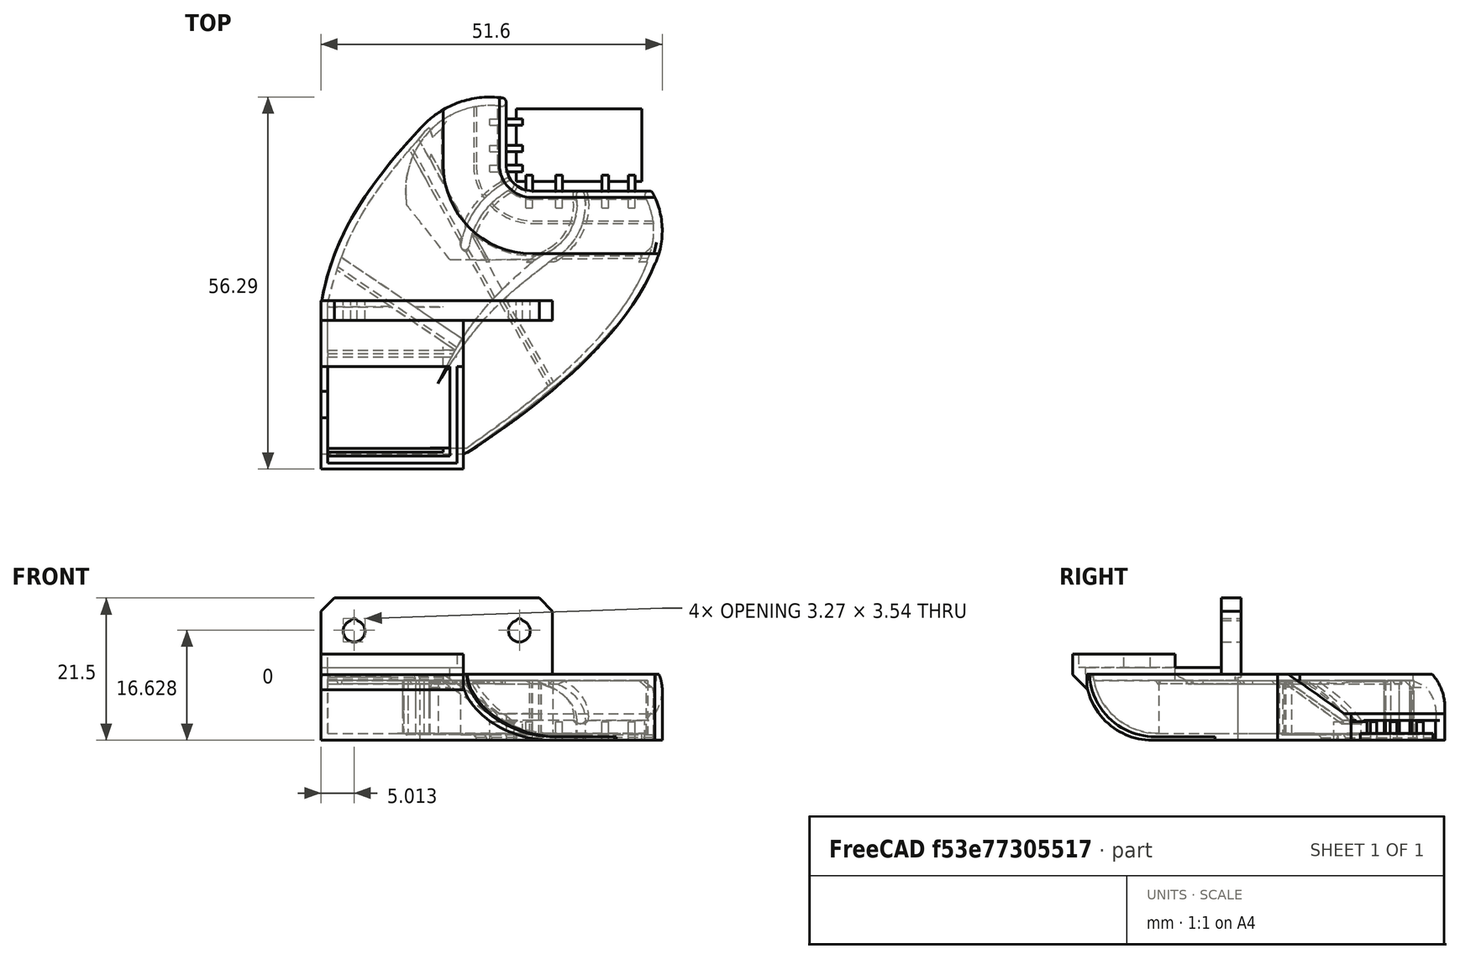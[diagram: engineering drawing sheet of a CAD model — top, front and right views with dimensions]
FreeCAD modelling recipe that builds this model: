
FCSTD DOCUMENT  (FreeCAD 0.18R16146 (Git))
Label: titanduct-v6-block
License: All rights reserved
LicenseURL: http://en.wikipedia.org/wiki/All_rights_reserved
objects: Part::Box×43, Part::Cut×25, Part::Feature×15, Part::MultiFuse×13, Part::Chamfer×10, Part::Cylinder×6, Part::Fillet×6
note: 118 computed .brp shape members not serialized (recipe doc carries the construction recipe); baked Part::Feature solids carry a one-line shape summary decoded from their .brp

FEATURE [Part::Feature] Part__Feature034001  label="duct001"
  Placement = pos=(4.485,21.775,-6.0908e-11) rot=(0,0,-1;0.785398rad)
  shape: bbox 54.56 x 52.76 x 17.07 mm, 140 faces (baked)
FEATURE [Part::Box] Box  label="Cube"
  AttacherType = Attacher::AttachEngine3D
  Height = 10
  Length = 42
  Placement = pos=(-35,-33,10) rot=(0,0,1;0rad)
  Width = 47
FEATURE [Part::Cut] Cut
  Base = -> Part__Feature034001
  Tool = -> Box
FEATURE [Part::Box] Box001  label="Cube001"
  AttacherType = Attacher::AttachEngine3D
  Height = 31
  Length = 50
  Placement = pos=(-35,-32,-4) rot=(0,0,1;0rad)
  Width = 31
FEATURE [Part::Cut] Cut001
  Base = -> Cut
  Tool = -> Box001
FEATURE [Part::Box] Box002  label="Cube002"
  AttacherType = Attacher::AttachEngine3D
  Height = 16
  Length = 10
  Placement = pos=(-33.8,-4,0) rot=(0,0,1;0rad)
  Width = 10
FEATURE [Part::Cut] Cut002
  Base = -> Cut001
  Placement = pos=(-2.5,3.3,-9) rot=(0,0,1;0rad)
  Tool = -> Box002
FEATURE [Part::Box] Box005  label="Cube005"
  AttacherType = Attacher::AttachEngine3D
  Height = 10
  Length = 35
  Width = 3
FEATURE [Part::Cylinder] Cylinder
  Angle = 360
  AttacherType = Attacher::AttachEngine3D
  Height = 10
  Placement = pos=(5,1e-15,5) rot=(-1,0,0;1.5708rad)
  Radius = 1.65
FEATURE [Part::Cylinder] Cylinder001
  Angle = 360
  AttacherType = Attacher::AttachEngine3D
  Height = 10
  Placement = pos=(30,1e-15,5) rot=(-1,0,0;1.5708rad)
  Radius = 1.65
FEATURE [Part::Cylinder] Cylinder002
  Angle = 360
  AttacherType = Attacher::AttachEngine3D
  Height = 10
  Placement = pos=(30,1e-15,5) rot=(-1,0,0;1.5708rad)
  Radius = 0.5
FEATURE [Part::Cylinder] Cylinder003
  Angle = 360
  AttacherType = Attacher::AttachEngine3D
  Height = 10
  Placement = pos=(5,1e-15,5) rot=(-1,0,0;1.5708rad)
  Radius = 0.5
FEATURE [Part::MultiFuse] Fusion001
  Shapes = -> [Cylinder001,Cylinder]
FEATURE [Part::MultiFuse] Fusion002
  Placement = pos=(0,0,1.4) rot=(0,0,1;0rad)
  Shapes = -> [Cylinder003,Cylinder002]
FEATURE [Part::MultiFuse] Fusion003
  Shapes = -> [Fusion002,Fusion001]
FEATURE [Part::Chamfer] Chamfer001
  Base = -> Box005
  Edges = 2 edges r=2: [Edge2,Edge6]
FEATURE [Part::Cut] Cut003  label="mounter"
  Base = -> Chamfer001
  Placement = pos=(-38,-6.5,11) rot=(0,0,1;0rad)
  Tool = -> Fusion003
FEATURE [Part::Box] Box014  label="Cube014"
  AttacherType = Attacher::AttachEngine3D
  Height = 3
  Length = 1
  Placement = pos=(-38,-29,9.5) rot=(0,0,1;0rad)
  Width = 7.75
FEATURE [Part::Box] Box015  label="Cube015"
  AttacherType = Attacher::AttachEngine3D
  Height = 3
  Length = 1
  Placement = pos=(-38,-17.25,9.5) rot=(0,0,1;0rad)
  Width = 3.75
FEATURE [Part::Box] Box016  label="Cube016"
  AttacherType = Attacher::AttachEngine3D
  Height = 1
  Length = 21.5
  Placement = pos=(-2.5,-38,-1) rot=(0,0,1;0rad)
  Width = 18.5
FEATURE [Part::Box] Box017  label="Cube017"
  AttacherType = Attacher::AttachEngine3D
  Height = 1.5
  Length = 21.5
  Placement = pos=(-38,-11.5,9) rot=(0,0,1;0rad)
  Width = 8
FEATURE [Part::Box] Box018  label="Cube018"
  AttacherType = Attacher::AttachEngine3D
  Height = 1
  Length = 18.5
  Placement = pos=(-1.5,-36,-1) rot=(0,0,1;0rad)
  Width = 13.5
FEATURE [Part::Feature] Body001001  label="Body002"
  Placement = pos=(0,0,-9) rot=(0,0,1;0rad)
  shape: bbox 32 x 33 x 12 mm, 6 faces (baked)
FEATURE [Part::Feature] Body001002  label="Body003"
  Placement = pos=(0,0,-9) rot=(0,0,1;0rad)
  shape: bbox 16 x 26.5 x 13 mm, 6 faces (baked)
FEATURE [Part::Box] Box021  label="Cube021"
  AttacherType = Attacher::AttachEngine3D
  Height = 18
  Length = 52
  Placement = pos=(-38,-28,-9) rot=(0,0,1;0rad)
  Width = 2
FEATURE [Part::Box] Box022  label="Cube022"
  AttacherType = Attacher::AttachEngine3D
  Height = 1
  Length = 52
  Placement = pos=(-38,-27,-9) rot=(0,0,1;0rad)
  Width = 20
FEATURE [Part::Feature] Fusion004002003
  shape: bbox 52 x 20 x 18 mm, 8 faces (baked)
FEATURE [Part::Fillet] Fillet
  Base = -> Fusion004002003
  Edges = 1 edges r=10: [Edge7]
FEATURE [Part::Fillet] Fillet002
  Base = -> Fillet
  Edges = 1 edges r=10: [Edge21]
FEATURE [Part::MultiFuse] Fusion
  Shapes = -> [Box021,Box022]
FEATURE [Part::Fillet] Fillet003
  Base = -> Fusion
  Edges = 1 edges r=10: [Edge11]
  Placement = pos=(0,-0.5,-0.5) rot=(0,0,1;0rad)
FEATURE [Part::Feature] Fillet003001  label="Fillet004"
  Placement = pos=(0,-0.5,-0.5) rot=(0,0,1;0rad)
  shape: bbox 52 x 21 x 18 mm, 15 faces (baked)
FEATURE [Part::Cut] Cut005
  Base = -> Body001001
  Tool = -> Fillet003001
FEATURE [Part::Box] Box023  label="Cube023"
  AttacherType = Attacher::AttachEngine3D
  Height = 18
  Length = 1
  Placement = pos=(-38,-27,-9) rot=(0,0,1;0rad)
  Width = 23
FEATURE [Part::Box] Box024  label="Cube024"
  AttacherType = Attacher::AttachEngine3D
  Height = 10
  Length = 42
  Placement = pos=(-43,-12,1) rot=(0,0,1;0rad)
  Width = 41
FEATURE [Part::Box] Box025  label="Cube025"
  AttacherType = Attacher::AttachEngine3D
  Height = 10
  Length = 42
  Placement = pos=(-18,-32,1) rot=(0,0,1;0rad)
  Width = 41
FEATURE [Part::Cut] Cut007
  Base = -> Cut005
  Tool = -> Box025
FEATURE [Part::Chamfer] Chamfer
  Base = -> Cut007
  Edges = 1 edges r=2: [Edge10]
FEATURE [Part::Cut] Cut008
  Base = -> Body001002
  Tool = -> Box024
FEATURE [Part::Chamfer] Chamfer008
  Base = -> Chamfer
  Edges = 1 edges r=0.4: [Edge1]
FEATURE [Part::Feature] Body001001001  label="Body004"
  Placement = pos=(1,0,-11) rot=(0,0,1;0rad)
  shape: bbox 32 x 33 x 12 mm, 6 faces (baked)
FEATURE [Part::Feature] Body001001002  label="Body005"
  Placement = pos=(1,0,-2) rot=(0,0,1;0rad)
  shape: bbox 32 x 33 x 12 mm, 6 faces (baked)
FEATURE [Part::MultiFuse] Fusion004002004
  Shapes = -> [Body001001002,Body001001001]
FEATURE [Part::Cut] Cut009
  Base = -> Fillet002
  Tool = -> Fusion004002004
FEATURE [Part::Feature] Pad002001  label="Pad003"
  Placement = pos=(0,0,-13) rot=(0,0,1;0rad)
  shape: bbox 37.34 x 24.4 x 27 mm, 14 faces (baked)
FEATURE [Part::Cut] Cut010
  Base = -> Cut009
  Tool = -> Pad002001
FEATURE [Part::Feature] Pad002002001  label="Pad002003"
  shape: bbox 50.43 x 49.62 x 1 mm, 36 faces (baked)
FEATURE [Part::Cut] Cut011
  Base = -> Box023
  Tool = -> Fillet003
FEATURE [Part::Feature] Fusion004002006001  label="Fusion004002007"
  shape: bbox 20.5 x 11 x 10 mm, 8 faces (baked)
FEATURE [Part::Fillet] Fillet003002
  Base = -> Fusion004002006001
  Edges = 1 edges r=5: [Edge7]
FEATURE [Part::Fillet] Fillet003003
  Base = -> Fillet003002
  Edges = 1 edges r=5: [Edge21]
FEATURE [Part::Box] Box028  label="Cube028"
  AttacherType = Attacher::AttachEngine3D
  Height = 10
  Length = 1
  Placement = pos=(-19.5,-27,0) rot=(0,0,1;0rad)
  Width = 23
FEATURE [Part::Box] Box029  label="Cube029"
  AttacherType = Attacher::AttachEngine3D
  Height = 10
  Length = 7
  Placement = pos=(-19.5,-27,1) rot=(0,0,1;0rad)
  Width = 23
FEATURE [Part::Cut] Cut012
  Base = -> Cut010
  Tool = -> Box029
FEATURE [Part::Box] Box030  label="Cube030"
  AttacherType = Attacher::AttachEngine3D
  Height = 1
  Length = 3
  Placement = pos=(-19.5,-27,0) rot=(0,0,1;0rad)
  Width = 23
FEATURE [Part::Box] Box031  label="Cube031"
  AttacherType = Attacher::AttachEngine3D
  Height = 10
  Length = 1
  Placement = pos=(-18.5,-27,1) rot=(0,0,1;0rad)
  Width = 23
FEATURE [Part::Cut] Cut013
  Base = -> Fillet003003
  Tool = -> Box031
FEATURE [Part::MultiFuse] Fusion004002006002
  Shapes = -> [Box028,Box030]
FEATURE [Part::Feature] Body001001003  label="Body006"
  Placement = pos=(0,0,-8) rot=(0,0,1;0rad)
  shape: bbox 7.895 x 21.33 x 5 mm, 13 faces (baked)
FEATURE [Part::Feature] Body001001004  label="Body007"
  Placement = pos=(0,0,-5) rot=(0,0,1;0rad)
  shape: bbox 7.895 x 21.33 x 5 mm, 13 faces (baked)
FEATURE [Part::Cut] Cut014
  Base = -> Cut002
  Tool = -> Body001001003
FEATURE [Part::Cut] Cut015
  Base = -> Cut014
  Tool = -> Body001001004
FEATURE [Part::Box] Box032  label="Cube032"
  AttacherType = Attacher::AttachEngine3D
  Height = 2
  Length = 10
  Placement = pos=(-28,-1,-8) rot=(0,0,1;0rad)
  Width = 15
FEATURE [Part::Cut] Cut016
  Base = -> Cut015
  Tool = -> Box032
FEATURE [Part::Feature] Body001001005  label="Body008"
  Placement = pos=(0,0,-9) rot=(0,0,1;0rad)
  shape: bbox 49.61 x 30.51 x 1 mm, 16 faces (baked)
FEATURE [Part::Box] Box033  label="Cube033"
  AttacherType = Attacher::AttachEngine3D
  Height = 1
  Length = 4
  Placement = pos=(-27,2,-9) rot=(0,0,1;0rad)
  Width = 4
FEATURE [Part::MultiFuse] Fusion004002006003
  Shapes = -> [Body001001005,Box033]
FEATURE [Part::Feature] Body001001006  label="Body009"
  Placement = pos=(0,0,-8.5) rot=(0,0,1;0rad)
  shape: bbox 17.67 x 19.56 x 20 mm, 5 faces (baked)
FEATURE [Part::Chamfer] Chamfer009
  Base = -> Body001001006
  Edges = 1 edges: [Edge1 r1=2 r2=0.2]
FEATURE [Part::Box] Box034  label="Cube034"
  AttacherType = Attacher::AttachEngine3D
  Height = 33
  Length = 31
  Placement = pos=(-29,-12.5,0.5) rot=(0,0,1;0rad)
  Width = 29
FEATURE [Part::Cut] Cut017
  Base = -> Chamfer009
  Tool = -> Box034
FEATURE [Part::Box] Box035  label="Cube035"
  AttacherType = Attacher::AttachEngine3D
  Height = 11
  Length = 18
  Placement = pos=(-29,-19.5,8.5) rot=(0,0,1;0rad)
  Width = 10
FEATURE [Part::Box] Box036  label="Cube036"
  AttacherType = Attacher::AttachEngine3D
  Height = 32
  Length = 18
  Placement = pos=(-29,-26,-9) rot=(0,0,1;0rad)
  Width = 10
FEATURE [Part::Cut] Cut018
  Base = -> Cut017
  Tool = -> Box036
FEATURE [Part::Box] Box037  label="Cube037"
  AttacherType = Attacher::AttachEngine3D
  Height = 15
  Length = 10
  Placement = pos=(-24,-13.5,5.5) rot=(0,0,1;0rad)
  Width = 10
FEATURE [Part::Cut] Cut019
  Base = -> Cut018
  Tool = -> Box035
FEATURE [Part::Fillet] Fillet003004
  Base = -> Box037
  Edges = 1 edges r=5: [Edge9]
  Placement = pos=(0,-2,-5.5) rot=(0,0,1;0rad)
FEATURE [Part::Cut] Cut020
  Base = -> Cut019
  Tool = -> Fillet003004
FEATURE [Part::Box] Box038  label="Cube038"
  AttacherType = Attacher::AttachEngine3D
  Height = 1
  Length = 2
  Placement = pos=(-17.3285,-11.2731,-0.5) rot=(0,0,1;0.977384rad)
  Width = 23
FEATURE [Part::Box] Box039  label="Cube039"
  AttacherType = Attacher::AttachEngine3D
  Height = 1
  Length = 2
  Placement = pos=(-11.7994,-3.80881,-0.5) rot=(0,0,1;0.506145rad)
  Width = 27
FEATURE [Part::Chamfer] Chamfer010
  Base = -> Box038
  Edges = 1 edges r=0.5: [Edge4]
FEATURE [Part::Chamfer] Chamfer011
  Base = -> Box039
  Edges = 1 edges r=0.5: [Edge4]
FEATURE [Part::Box] Box040  label="Cube040"
  AttacherType = Attacher::AttachEngine3D
  Height = 3
  Length = 35
  Placement = pos=(-38,-6.5,9) rot=(0,0,1;0rad)
  Width = 3
FEATURE [Part::Cylinder] Cylinder004
  Angle = 360
  AttacherType = Attacher::AttachEngine3D
  Height = 35
  Placement = pos=(-9,-8,3) rot=(0,-1,0;1.5708rad)
  Radius = 1
FEATURE [Part::Cylinder] Cylinder005
  Angle = 360
  AttacherType = Attacher::AttachEngine3D
  Height = 35
  Placement = pos=(-9,-8,3) rot=(0,-1,0;1.5708rad)
  Radius = 1
FEATURE [Part::Cut] Cut021
  Base = -> Cut011
  Tool = -> Cylinder004
FEATURE [Part::Cut] Cut022
  Base = -> Fusion004002006002
  Tool = -> Cylinder005
FEATURE [Part::Box] Box043  label="Cube043"
  AttacherType = Attacher::AttachEngine3D
  Height = 1
  Length = 20
  Placement = pos=(-37.5,-12,-0.5) rot=(0,0,1;0rad)
  Width = 1
FEATURE [Part::Chamfer] Chamfer016
  Base = -> Box043
  Edges = 1 edges r=0.5: [Edge9]
FEATURE [Part::Box] Box044  label="Cube044"
  AttacherType = Attacher::AttachEngine3D
  Height = 1
  Length = 15.5
  Placement = pos=(-11.2452,-3.31699,-0.5) rot=(0,0,-1;1.0472rad)
  Width = 1
FEATURE [Part::Chamfer] Chamfer017
  Base = -> Box044
  Edges = 1 edges r=0.5: [Edge9]
FEATURE [Part::MultiFuse] Fusion004002006006
  Placement = pos=(0,0,2.5) rot=(0,0,1;0rad)
  Shapes = -> [Cut008,Chamfer008,Pad002002001,Cut012,Cut013,Cut016,Fusion004002006003,Cut020,Chamfer010,Chamfer011,Cut021,Cut022,Chamfer016,Chamfer017]
FEATURE [Part::Box] Box046  label="Cube046"
  AttacherType = Attacher::AttachEngine3D
  Height = 23
  Length = 52
  Placement = pos=(-38,-38.5,7.5) rot=(0,0,1;0rad)
  Width = 59
FEATURE [Part::Cut] Cut023
  Base = -> Fusion004002006006
  Tool = -> Box046
FEATURE [Part::Box] Box047  label="Cube047"
  AttacherType = Attacher::AttachEngine3D
  Height = 23
  Length = 52
  Placement = pos=(-38,-38.5,3.5) rot=(0,0,1;0rad)
  Width = 59
FEATURE [Part::Cut] Cut025
  Base = -> Cut023
  Placement = pos=(0,0,6) rot=(0,0,1;0rad)
  Tool = -> Box047
FEATURE [Part::Box] Box048  label="Cube048"
  AttacherType = Attacher::AttachEngine3D
  Height = 3
  Length = 21.5
  Placement = pos=(-38,-29,9.5) rot=(0,0,1;0rad)
  Width = 0.9
FEATURE [Part::Box] Box049  label="Cube049"
  AttacherType = Attacher::AttachEngine3D
  Height = 3
  Length = 0.9
  Placement = pos=(-17.4,-29,9.5) rot=(0,0,1;0rad)
  Width = 15.5
FEATURE [Part::Box] Box052  label="Cube052"
  AttacherType = Attacher::AttachEngine3D
  Height = 2
  Length = 3
  Placement = pos=(-21.5,-25.8,8.5) rot=(0,0,1;0rad)
  Width = 12.3
FEATURE [Part::Chamfer] Chamfer020
  Base = -> Cut025
  Edges = 1 edges r=0.5: [Edge164]
FEATURE [Part::Cut] Cut024005005
  Base = -> Chamfer020
  Tool = -> Box052
FEATURE [Part::Cut] Cut024005006
  Base = -> Box016
  Placement = pos=(-35.5,9,10.5) rot=(0,0,1;0rad)
  Tool = -> Box018
FEATURE [Part::Box] Box053  label="Cube053"
  AttacherType = Attacher::AttachEngine3D
  Height = 2.5
  Length = 21.5
  Placement = pos=(-38,-29,7) rot=(0,0,1;0rad)
  Width = 2.5
FEATURE [Part::Chamfer] Chamfer022002
  Base = -> Box053
  Edges = 1 edges r=2.4: [Edge9]
FEATURE [Part::MultiFuse] Fusion004002006007
  Shapes = -> [Box048,Box049,Box015,Box014,Cut003,Box040,Box017,Cut024005006]
FEATURE [Part::MultiFuse] Fusion004002006008
  Shapes = -> [Fusion004002006007,Chamfer022002]
FEATURE [Part::MultiFuse] Fusion004002006009  label="rev-1"
  Shapes = -> [Fusion004002006008,Cut024005005]
FEATURE [Part::Feature] Fusion004002006009001  label="rev-1-exp"
  shape: bbox 52.52 x 56.29 x 21.62 mm, 191 faces (baked)
FEATURE [Part::Box] Box054  label="Cube054"
  AttacherType = Attacher::AttachEngine3D
  Height = 2.8
  Length = 1
  Placement = pos=(4.5,10.5,-0.5) rot=(0,0,1;0rad)
  Width = 5
FEATURE [Part::Box] Box055  label="Cube055"
  AttacherType = Attacher::AttachEngine3D
  Height = 2.8
  Length = 1
  Placement = pos=(8.5,10.5,-0.5) rot=(0,0,1;0rad)
  Width = 5
FEATURE [Part::Box] Box056  label="Cube056"
  AttacherType = Attacher::AttachEngine3D
  Height = 2.8
  Length = 1
  Placement = pos=(-2.5,10.5,-0.5) rot=(0,0,1;0rad)
  Width = 5
FEATURE [Part::Box] Box057  label="Cube057"
  AttacherType = Attacher::AttachEngine3D
  Height = 2.8
  Length = 1
  Placement = pos=(-7,10.5,-0.5) rot=(0,0,1;0rad)
  Width = 5
FEATURE [Part::Box] Box058  label="Cube058"
  AttacherType = Attacher::AttachEngine3D
  Height = 2.8
  Length = 5
  Placement = pos=(-12.5,16,-0.5) rot=(0,0,1;0rad)
  Width = 1
FEATURE [Part::Box] Box059  label="Cube059"
  AttacherType = Attacher::AttachEngine3D
  Height = 2.8
  Length = 5
  Placement = pos=(-12.5,19,-0.5) rot=(0,0,1;0rad)
  Width = 1
FEATURE [Part::Box] Box060  label="Cube060"
  AttacherType = Attacher::AttachEngine3D
  Height = 2.8
  Length = 5
  Placement = pos=(-12.5,23,-0.5) rot=(0,0,1;0rad)
  Width = 1
FEATURE [Part::Box] Box061  label="Cube061"
  AttacherType = Attacher::AttachEngine3D
  Height = 1
  Length = 19
  Placement = pos=(-8.5,14.5,-0.5) rot=(0,0,1;0rad)
  Width = 11
FEATURE [Part::MultiFuse] Fusion004002006009002  label="print-support"
  Shapes = -> [Box054,Box055,Box056,Box057,Box059,Box058,Box060,Box061]
FEATURE [Part::MultiFuse] Fusion004002006009003  label="rev1-exp-support"
  Shapes = -> [Fusion004002006009002,Fusion004002006009001]
